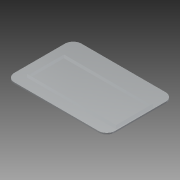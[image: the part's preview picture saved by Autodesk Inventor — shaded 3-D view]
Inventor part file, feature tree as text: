
AUTODESK INVENTOR PART (.ipt)
format: ipt  version: 2014 (Build 180170000, 170)  size: 127,488 bytes
history: native  units: mm
features: reference x12, extrude x2, sketch x2
ambient origin geometry x8: Origin, YZ Plane, XZ Plane, XY Plane, X Axis, Y Axis, Z Axis, Center Point
bodies: Solid1 (feature_tree)
feature tree (16):
  extrude  "Extrusion1"  Depth=51.0mm
  extrude  "Extrusion2"  Depth=53.0mm
  sketch  "Sketch1"  dims[d0=0.8mm d1=0.0mm d2=51.0mm]
  reference  "Reference1"
  reference  "Reference2"
  reference  "Reference3"
  reference  "Reference4"
  reference  "Reference5"
  reference  "Reference6"
  reference  "Reference7"
  reference  "Reference8"
  reference  "Reference9"
  reference  "Reference10"
  reference  "Reference11"
  reference  "Reference12"
  sketch  "Sketch2"  dims[d3=20.0mm d4=53.0mm d5=22.0mm d6=2.0mm d7=0.0mm d8=60.0mm d9=40.0mm]
